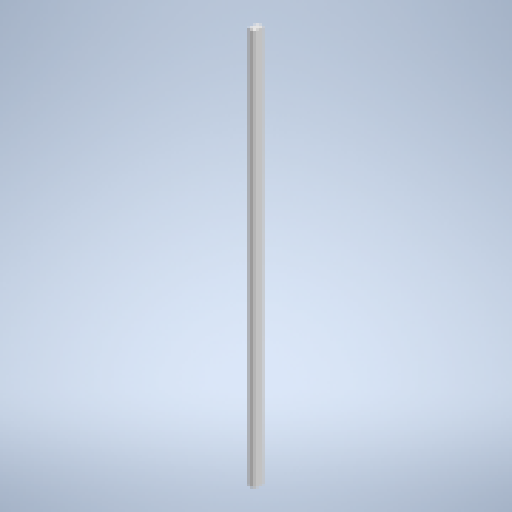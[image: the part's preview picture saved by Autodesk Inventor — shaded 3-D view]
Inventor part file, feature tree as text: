
AUTODESK INVENTOR PART (.ipt)
format: ipt  version: 2023 (Build 270158000, 158)  size: 3,473,408 bytes
history: native  units: mm
features: other x14, sketch x6, extrude x5, chamfer x1
ambient origin geometry x8: Origin, YZ Plane, XZ Plane, XY Plane, X Axis, Y Axis, Z Axis, Center Point
bodies: Solide1 (feature_tree)
feature tree (26):
  extrude  "Extrusion1"  Depth=2.0mm TaperAngle=0.0deg
  sketch  "Esquisse2"
  other  "Plan de construction1"
  extrude  "Extrusion2"  Depth=103.75mm TaperAngle=0.0deg
  other  "Plan de construction2"
  extrude  "Extrusion3"  Depth=10.0mm TaperAngle=0.0deg
  extrude  "Extrusion4"  Depth=10.0mm TaperAngle=0.0deg
  chamfer  "Chanfrein1"  Distance=0.4mm Angle=45.0deg
  sketch  "Esquisse5"
  sketch  "Esquisse7"
  other  "Gravure1"
  extrude  "Extrusion5"  Depth=0.5mm TaperAngle=0.0deg
  sketch  "Esquisse1"
  other  "Référence2"
  other  "Référence3"
  other  "Référence4"
  sketch  "Esquisse3"
  other  "Référence5"
  other  "Référence6"
  sketch  "Esquisse4"
  other  "Référence7"
  other  "Référence8"
  other  "Référence9"
  other  "<userpath>\Desktop\PE-SM\3D\Ensemble.iam"
  other  "Ensemble.iam"
  other  "PE:1"
